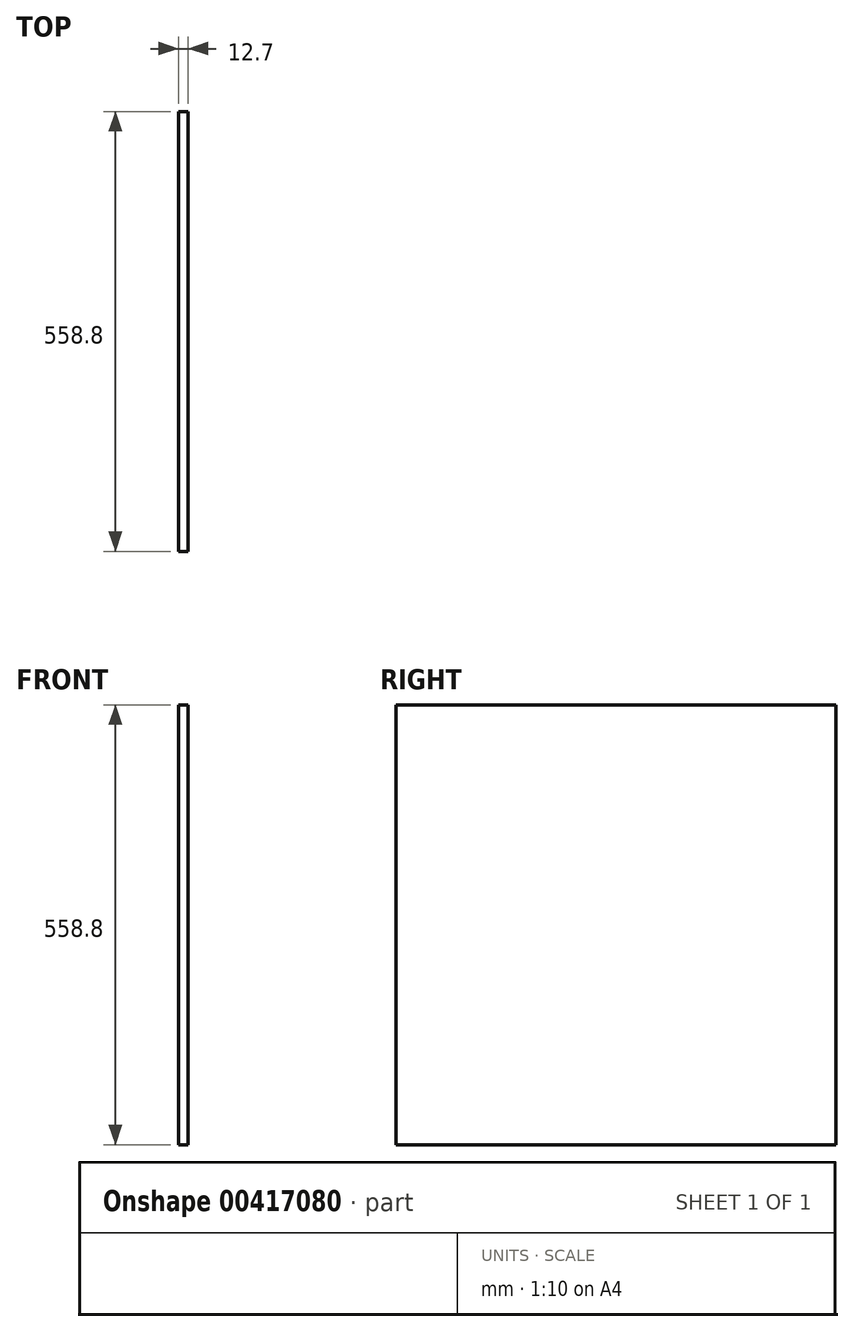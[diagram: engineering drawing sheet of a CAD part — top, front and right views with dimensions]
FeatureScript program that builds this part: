
annotation { "Feature Type Name" : "Feature", "Feature Type Description" : "" }
export const myFeature = defineFeature(function(context is Context, id is Id, definition is map)
    precondition{}
    {
        {
            var Q0;
            Q0=qCreatedBy(makeId("Right.planeOp"),FACE);
            var sketch = newSketch(context, id + "F0", { "sketchPlane" : qUnion([Q0])});
            skLineSegment(sketch, "E0.bottom", {"start": v(0, 0) * mm, "end": v(-558.8, 0) * mm});
            skLineSegment(sketch, "E0.top", {"start": v(0, -558.8) * mm, "end": v(-558.8, -558.8) * mm});
            skLineSegment(sketch, "E0.left", {"start": v(0, 0) * mm, "end": v(0, -558.8) * mm});
            skLineSegment(sketch, "E0.right", {"start": v(-558.8, 0) * mm, "end": v(-558.8, -558.8) * mm});
            skSolve(sketch);
        }
        {
            var Q0;
            Q0 = qSketchRegion(id + "F0", true);
            extrude(context, id + "F1", {"entities" : qUnion([Q0]), "depth" : 12.7 * mm});
        }
    });
